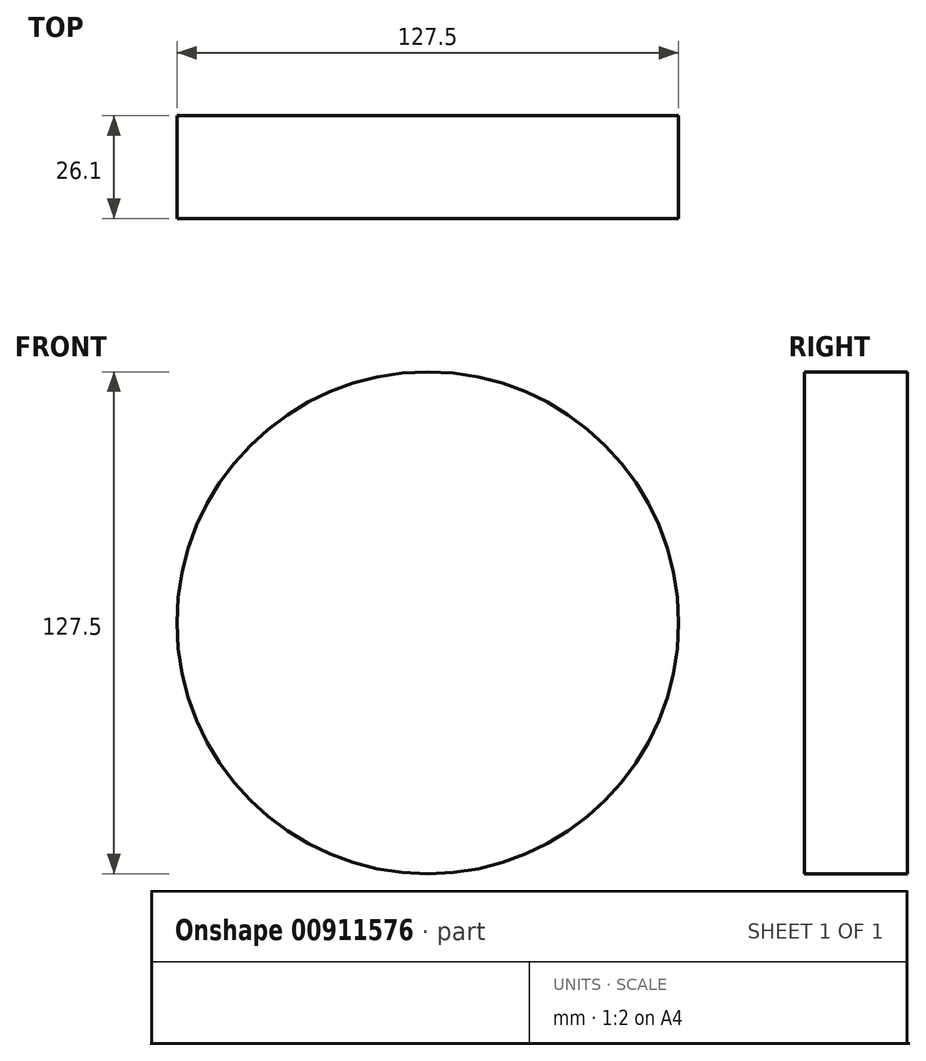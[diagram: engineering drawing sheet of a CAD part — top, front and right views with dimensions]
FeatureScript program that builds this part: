
annotation { "Feature Type Name" : "Feature", "Feature Type Description" : "" }
export const myFeature = defineFeature(function(context is Context, id is Id, definition is map)
    precondition{}
    {
        {
            var Q0;
            Q0=qCreatedBy(makeId("Front.planeOp"),FACE);
            var sketch = newSketch(context, id + "F0", { "sketchPlane" : qUnion([Q0])});
            skCircle(sketch, "E0", {"center": v(0, 0) * mm, "radius": 63.75 * mm});
            skSolve(sketch);
        }
        {
            var Q0;
            Q0=makeQuery(id+"F0.imprint","IMPRINT",FACE,{"disambiguationData":[TD([[makeQuery(id+"F0.imprint","IMPRINT",EDGE,{"derivedFrom":sQuery(id+"F0.wireOp",EDGE,"E0")}),1.0]])]});
            extrude(context, id + "F1", {"entities" : qUnion([Q0]), "depth" : 26.1 * mm, "offsetDistance" : 25 * mm});
        }
    });
